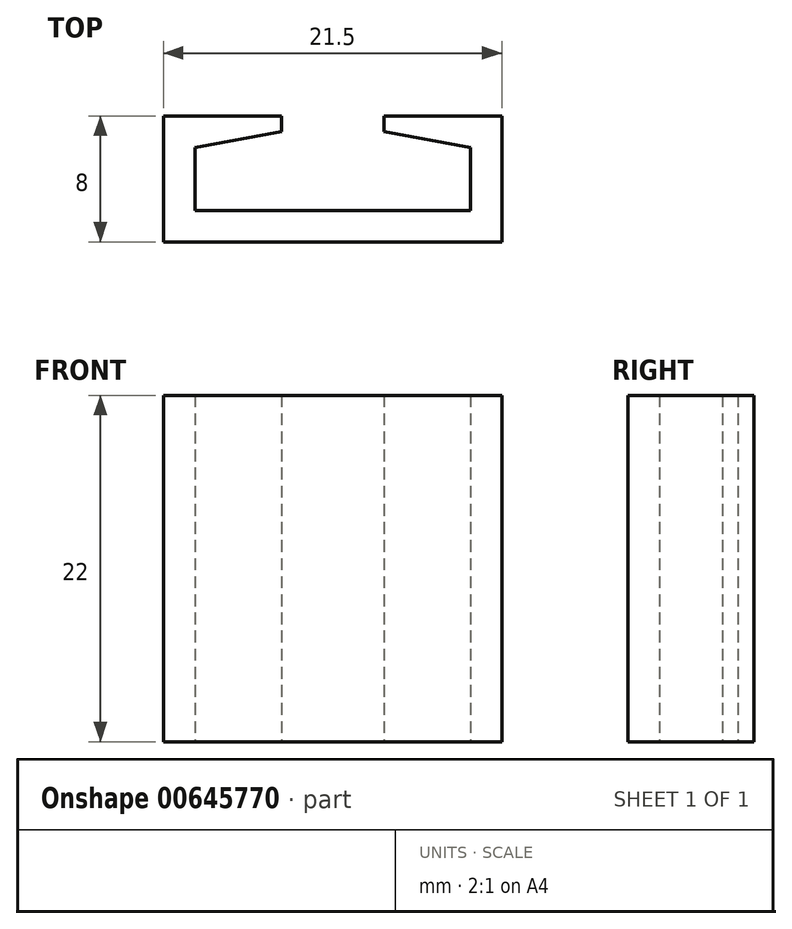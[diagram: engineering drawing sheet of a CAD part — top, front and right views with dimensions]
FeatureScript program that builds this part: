
annotation { "Feature Type Name" : "Feature", "Feature Type Description" : "" }
export const myFeature = defineFeature(function(context is Context, id is Id, definition is map)
    precondition{}
    {
        {
            var Q0;
            Q0=qCreatedBy(makeId("Top.planeOp"),FACE);
            var sketch = newSketch(context, id + "F0", { "sketchPlane" : qUnion([Q0])});
            skLineSegment(sketch, "E0", {"start": v(-8.75, 0) * mm, "end": v(8.75, 0) * mm});
            skLineSegment(sketch, "E1", {"start": v(8.75, 0) * mm, "end": v(8.75, 4) * mm});
            skLineSegment(sketch, "E2", {"start": v(8.75, 4) * mm, "end": v(3.25, 5) * mm});
            skLineSegment(sketch, "E3", {"start": v(3.25, 5) * mm, "end": v(3.25, 6) * mm});
            skLineSegment(sketch, "E4", {"start": v(3.25, 6) * mm, "end": v(10.75, 6) * mm});
            skLineSegment(sketch, "E5", {"start": v(10.75, 6) * mm, "end": v(10.75, -2) * mm});
            skLineSegment(sketch, "E6", {"start": v(10.75, -2) * mm, "end": v(-10.75, -2) * mm});
            skLineSegment(sketch, "E7", {"start": v(-10.75, -2) * mm, "end": v(-10.75, 6) * mm});
            skLineSegment(sketch, "E8", {"start": v(-10.75, 6) * mm, "end": v(-3.25, 6) * mm});
            skLineSegment(sketch, "E9", {"start": v(-3.25, 6) * mm, "end": v(-3.25, 5) * mm});
            skLineSegment(sketch, "E10", {"start": v(-3.25, 5) * mm, "end": v(-8.75, 4) * mm});
            skLineSegment(sketch, "E11", {"start": v(-8.75, 4) * mm, "end": v(-8.75, 0) * mm});
            skSolve(sketch);
        }
        {
            var Q0;
            Q0=makeQuery(id+"F0.imprint","IMPRINT",FACE,{"disambiguationData":[TD([[makeQuery(id+"F0.imprint","IMPRINT",EDGE,{"derivedFrom":sQuery(id+"F0.wireOp",EDGE,"E0")}),-1.0]])]});
            extrude(context, id + "F1", {"entities" : qUnion([Q0]), "depth" : 22 * mm, "offsetDistance" : 25 * mm});
        }
    });
